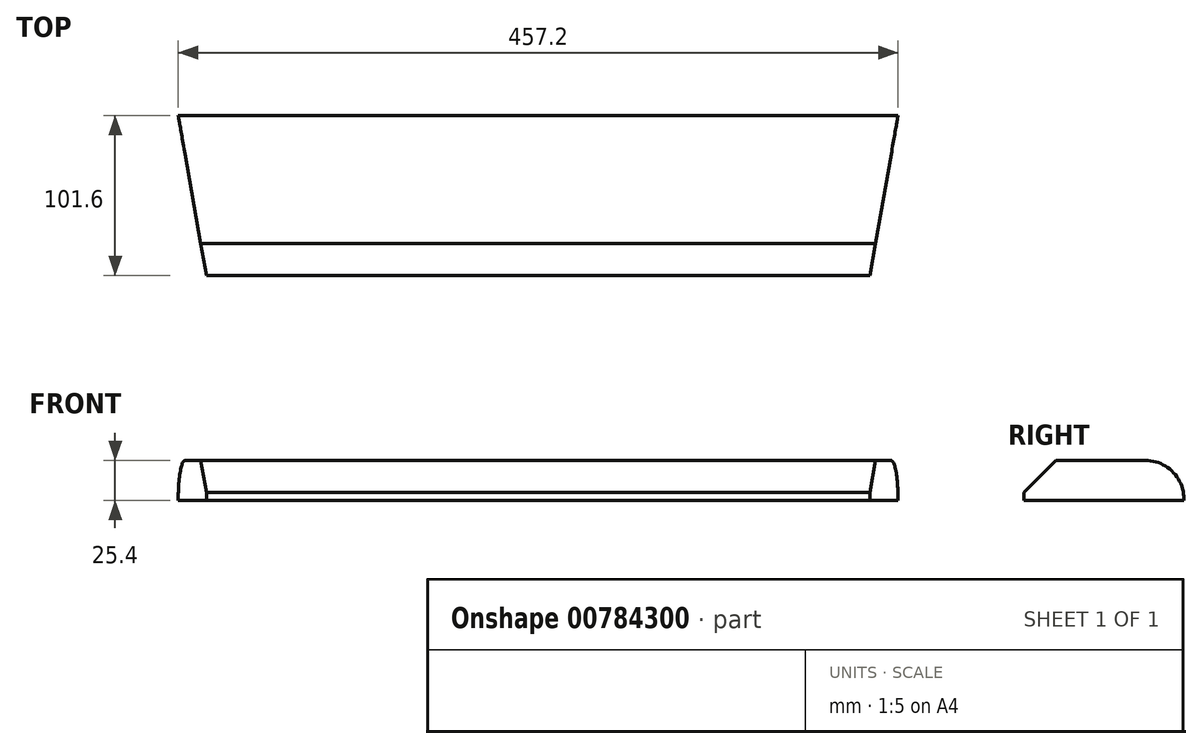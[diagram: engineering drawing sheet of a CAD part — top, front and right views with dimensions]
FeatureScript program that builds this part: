
annotation { "Feature Type Name" : "Feature", "Feature Type Description" : "" }
export const myFeature = defineFeature(function(context is Context, id is Id, definition is map)
    precondition{}
    {
        {
            var Q0;
            Q0=qCreatedBy(makeId("Right.planeOp"),FACE);
            var sketch = newSketch(context, id + "F0", { "sketchPlane" : qUnion([Q0])});
            skLineSegment(sketch, "E0.bottom", {"start": v(0, 0) * mm, "end": v(-101.6, 0) * mm});
            skLineSegment(sketch, "E0.top", {"start": v(0, 25.4) * mm, "end": v(-101.6, 25.4) * mm});
            skLineSegment(sketch, "E0.left", {"start": v(0, 0) * mm, "end": v(0, 25.4) * mm});
            skLineSegment(sketch, "E0.right", {"start": v(-101.6, 0) * mm, "end": v(-101.6, 25.4) * mm});
            skSolve(sketch);
        }
        {
            var Q0;
            Q0 = qSketchRegion(id + "F0", true);
            extrude(context, id + "F1", {"entities" : qUnion([Q0]), "depth" : 228.6 * mm, "offsetDistance" : 25.4 * mm});
        }
        {
            var Q0;
            Q0=makeQuery(id+"F1.opExtrude","SWEPT_EDGE",EDGE,{"disambiguationData":[OSD([sQuery(id+"F0.wireOp",EDGE,"E0.top"),sQuery(id+"F0.wireOp",EDGE,"E0.left")])]});
            fillet(context, id + "F2", {"entities" : qUnion([Q0]), "radius" : 24.54 * mm, "tangentPropagation" : true, "allowEdgeOverflow" : false});
        }
        {
            var Q0;
            Q0=makeQuery(id+"F1.opExtrude","SWEPT_FACE",FACE,{"disambiguationData":[OSD([sQuery(id+"F0.wireOp",EDGE,"E0.bottom")])]});
            var sketch = newSketch(context, id + "F3", { "sketchPlane" : qUnion([Q0])});
            skLineSegment(sketch, "E1.bottom", {"start": v(0, 0) * mm, "end": v(228.6, 0) * mm});
            skLineSegment(sketch, "E1.top", {"start": v(0, 101.6) * mm, "end": v(228.6, 101.6) * mm});
            skLineSegment(sketch, "E1.left", {"start": v(0, 0) * mm, "end": v(0, 101.6) * mm});
            skLineSegment(sketch, "E1.right", {"start": v(228.6, 0) * mm, "end": v(228.6, 101.6) * mm});
            skLineSegment(sketch, "E2", {"start": v(228.6, 0) * mm, "end": v(210.69, 101.6) * mm});
            skSolve(sketch);
        }
        {
            var Q0;
            {var subQ0=sQuery(id+"F3.wireOp",EDGE,"E1.right");Q0=makeQuery(id+"F3.imprint","IMPRINT",FACE,{"disambiguationData":[TD([[makeQuery(id+"F3.imprint","IMPRINT",EDGE,{"derivedFrom":subQ0}),1.0]])]});}
            extrude(context, id + "F4", {"entities" : qUnion([Q0]), "operationType" : NewBodyOperationType.REMOVE, "oppositeDirection" : true, "depth" : 25.4 * mm, "offsetDistance" : 25.4 * mm});
        }
        {
            var Q0;
            Q0=makeQuery(id+"F1.opExtrude","SWEPT_EDGE",EDGE,{"disambiguationData":[OSD([sQuery(id+"F0.wireOp",EDGE,"E0.top"),sQuery(id+"F0.wireOp",EDGE,"E0.right")])]});
            chamfer(context, id + "F5", {"entities" : qUnion([Q0]), "width" : 20.32 * mm, "tangentPropagation" : true});
        }
        {
            var Q0;
            Q0=makeQuery(id+"F1.opExtrude","SWEPT_BODY",BODY,{"disambiguationData":[OSD([sQuery(id+"F0.wireOp",EDGE,"E0.bottom"),sQuery(id+"F0.wireOp",EDGE,"E0.top"),sQuery(id+"F0.wireOp",EDGE,"E0.left"),sQuery(id+"F0.wireOp",EDGE,"E0.right")])]});
            var Q1;
            Q1=qCreatedBy(makeId("Right.planeOp"),FACE);
            mirror(context, id + "F6", {"operationType" : NewBodyOperationType.ADD, "entities" : qUnion([Q0]), "mirrorPlane" : qUnion([Q1])});
        }
    });
